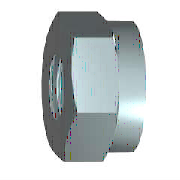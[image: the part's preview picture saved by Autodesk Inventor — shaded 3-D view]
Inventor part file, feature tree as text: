
AUTODESK INVENTOR PART (.ipt)
format: ipt  version: 2024.1 (Build 281209000, 209)  size: 177,664 bytes
history: native  units: mm (DEFAULTED — no unit token found)
features: extrude x1, chamfer x1, hole x1, other x1, plane x1
ambient origin geometry x7: Origin, YZ Plane, XZ Plane, X Axis, Y Axis, Z Axis, Center Point
bodies: Solid1 (feature_tree), Body (feature_tree)
feature tree (5):
  extrude  "Ring"  Depth=6.350853mm
  chamfer  "Chamfer1"  Distance=1.55mm
  hole  "Thread"  [1 undecoded]
  other  "Work Axis1"
  plane  "Work Plane1"
note: 1 required parameter value undecoded (feature->parameter linkage not recoverable at this tier; creation-order binding heuristic only, values carry confidence <= 0.55)
